# Revit family: SIMES_S.6420N_Shape
name_source: partatom
category: Lighting Fixtures
revit_build: Autodesk Revit 2016 (Build: 20150714_1515(x64)
units: mm (PartAtom-declared; Revit-internal decimal feet)

## family parameters
Cut with Voids When Loaded = No
Host = Face
Light Source = Yes
OmniClass Number = 23.80.70.14
OmniClass Title = Luminaries for External Lighting
Part Type = Normal
Room Calculation Point = No
Round Connector Dimension = Use Diameter
Shared = No

## types (1)
- SIMES_S.6420N_Shape
    Approval mark = CE, ENEC
    Assembly Code = D5020
    Color Filter = 16777215
    Color Rendering Index = CRI 70
    Colour Temperature = 4000
    Control Gear = electronic transformer
    Default Elevation = 1219 mm
    Description = SHAPE
Art. S.6420N
MODULES LED 4000K  230V CRI 70
Rated luminaire luminous flux: 211lm
Rated input power: 4.7W
Luminaire efficacy: 45lm/W
Electronic ballast 220÷240V 0/50/60Hz
CE - ENEC 03

PRODUCT TYPE
Wall mounted luminaire. IP rating IP 65
MATERIAL CHARACTERISTICS
Aluminium die cast housing in EN AB-47100 (low copper content) with high resistance against corrosion. Stone wash surface treatment prior to painting process. A4 grade Stainless Steel screws with 2,5-3% molybdenum content which increases the resistance against corrosion. Silicone gaskets. Painting Process : 3 Step Process
1) Surface treatment with BONDERITE. A heavy metal free chemical surface treatment containing ceramic nano particles giving a cohesive, inorganic and highly dense protective coating. 2) PRE POLYMERIZATION a process of introducing an epoxy primer with excellent characteristics to the paint which also offers very high resistance to oxidation due to its Zinc content. 3) POLYMERIZATION a process with the application of polyester powder with high resistance against UV rays and harsh weather conditions. Resistance test protection for Marine applications for 1200h.  Mechanical resistance IK 10
LIGHTING PERFORMANCE
Clear polycarbonate diffuser. LOR -- 
INSTALLATION AND MAINTENANCE
Protective cover with clip locking system. No visible screws. 
The fitting allows an adjustment of approximately 5° for the perfect alignment of the light beam with the window frame. 
WIRING
SHAPE Supplied with a 1,5m pre-wired H05RN-F cable. Isolation: CLASS I . Available colours: White (cod.01), Aluminium grey (cod.14). Weight: 0.5 Kg Glow Wire test: --
L.E.D circuit included.
SHAPE REGISTERED DESIGN
This luminaire contains built-in LED modules with energy class: A, A+, A++. In case of damage or malfunction please contact the manufacturer to receive additional instructions on how to replace and relative spare parts to order. The LED modules cannot be handled in the luminaire by the end user (Regulation UE 874/2012).
LED circuit boards are engineered accordingly to actual Lumen Maintenance regulation (LM80) and Technical Memorandum (TM21) where uniformity and quality of light is 50.000 hours referred to L70  B20 Ta 25°C.Lifecycle refers to LED circuit boards only, all others components of the luminaire are excluded.

EMERGENCY VERSIONS The fittings operates both on AC ( 50/60Hz ) and DC ( 0Hz ) voltage.
    Dimming Lamp Color Temperature Shift = <None>
    Frequency = 0/50/60Hz
    IFC Classification = Light Fixture
    IK Rating = IK 10
    Lamp = LED
    Lamp Light Flux = 428
    Lamp count = 1
    Last Update = 02/08/2018 10:55:39
    Lifetime = 50000 L70 B20 Ta 25°C
    Light Output Ratio = 100
    Luminous efficacy = 44,9
    Manufacturer = SIMES
    Masterformat 2014 Code = 26 56 00
    Masterformat 2014 Description = Exterior Lighting
    Model = S.6420N
    Mounting Place = Wall
    Mounting Type = Surface mounted
    NBS Reference Code = 49
    NBS Reference Description = Luminaries And Lamps
    OmniClass Code = 23-35 47 11
    OmniClass Description = Lighting Fixture
    Photometric Web File = S6420N.ies
    Product Group = wall-mounted luminaire
    Product Name = Shape
    Protection Class = Protection class I
    Protection Degree = IP 65
    System Light Flux = 211
    System Power = 4,69999980926514
    Tilt Angle = 90.00°
    Type Comments = SIMES S.p.A. - All rights reserved
    Type Image = shape.jpg
    UNSPSC Code = 3911
    URL = http://www.simes.it
    Uniclass 1.4 Code = YJ73
    Uniclass 1.4 Description = Luminaries and lamps
    Uniclass 2.0 Code = PR-49
    Uniclass 2.0 Description = Luminaries and lamps
    Uniclass 2015 Code = EF_70_80
    Uniclass 2015 Name = Lighting
    Uniformat II Code = D5020
    Uniformat II Description = Lighting & Branch Wiring
    Voltage = 220÷240V

## geometry (parser evidence)
native form markers: Sweep x2
no freeform markers — native parametric forms only
